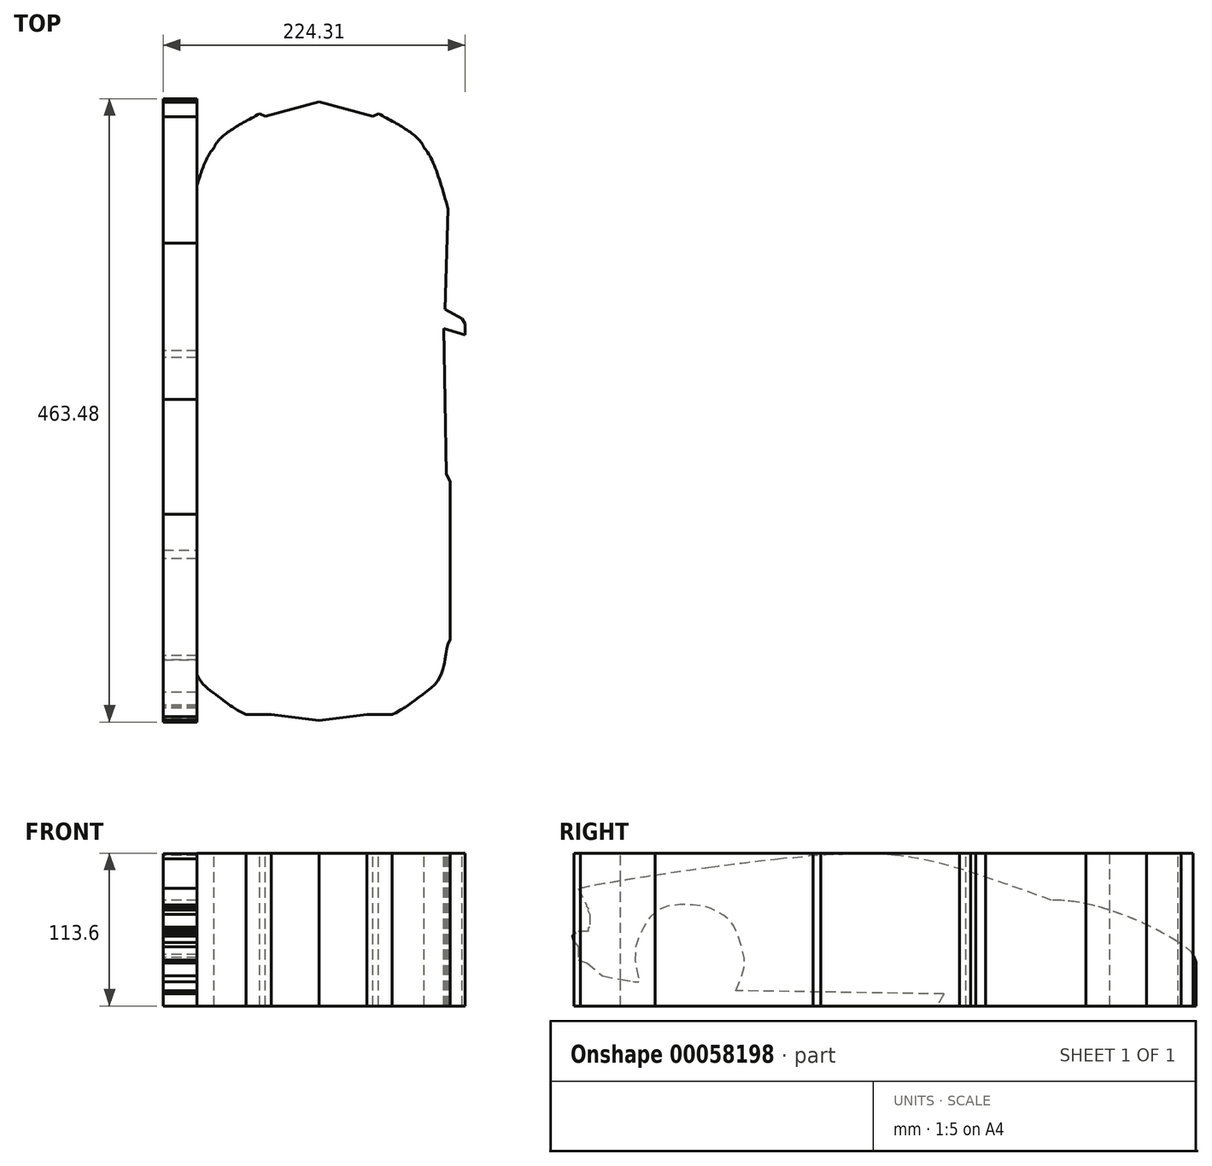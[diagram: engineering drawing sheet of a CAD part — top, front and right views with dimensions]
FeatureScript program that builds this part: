
annotation { "Feature Type Name" : "Feature", "Feature Type Description" : "" }
export const myFeature = defineFeature(function(context is Context, id is Id, definition is map)
    precondition{}
    {
        {
            var Q0;
            Q0=qCreatedBy(makeId("Right.planeOp"),FACE);
            var sketch = newSketch(context, id + "F0", { "sketchPlane" : qUnion([Q0])});
            skLineSegment(sketch, "E0.bottom", {"start": v(-232.28, 113.6) * mm, "end": v(232.28, 113.6) * mm});
            skLineSegment(sketch, "E0.top", {"start": v(-232.28, 0) * mm, "end": v(232.28, 0) * mm});
            skLineSegment(sketch, "E0.left", {"start": v(-232.28, 113.6) * mm, "end": v(-232.28, 0) * mm});
            skLineSegment(sketch, "E0.right", {"start": v(232.28, 113.6) * mm, "end": v(232.28, 0) * mm});
            skSolve(sketch);
        }
        {
            var Q0;
            Q0=makeQuery(id+"F0.imprint","IMPRINT",FACE,{"disambiguationData":[TD([[makeQuery(id+"F0.imprint","IMPRINT",EDGE,{"derivedFrom":sQuery(id+"F0.wireOp",EDGE,"E0.bottom")}),-1.0]])]});
            extrude(context, id + "F1", {"entities" : qUnion([Q0]), "depth" : 113.25 * mm});
        }
        {
            var Q0;
            Q0=makeQuery(id+"F1.opExtrude","CAP_FACE",FACE,{"disambiguationData":[OSD([sQuery(id+"F0.wireOp",EDGE,"E0.bottom"),sQuery(id+"F0.wireOp",EDGE,"E0.top"),sQuery(id+"F0.wireOp",EDGE,"E0.left"),sQuery(id+"F0.wireOp",EDGE,"E0.right")])],"isStart":true});
            extrude(context, id + "F2", {"entities" : qUnion([Q0]), "operationType" : NewBodyOperationType.ADD, "depth" : 113.25 * mm});
        }
        {
            var Q0;
            Q0=makeQuery(id+"F2.opExtrude","CAP_FACE",FACE,{"disambiguationData":[OSD([sQuery(id+"F0.wireOp",EDGE,"E0.bottom"),sQuery(id+"F0.wireOp",EDGE,"E0.top"),sQuery(id+"F0.wireOp",EDGE,"E0.left"),sQuery(id+"F0.wireOp",EDGE,"E0.right")])],"isStart":false});
            var sketch = newSketch(context, id + "F3", { "sketchPlane" : qUnion([Q0])});
            skFitSpline(sketch, "E1", {"points": [v(-163.56, 5.3) * mm, v(-228.72, 9.68) * mm, v(-231.1, 36.06) * mm, v(-229.78, 38.2) * mm, v(-227.25, 41.67) * mm, v(-112.37, 76.6) * mm, v(-33.22, -15.35) * mm], "startDerivative": vector(-140.7, 2.21) * mm, "endDerivative": vector(214.7, -339.45) * mm});
            skFitSpline(sketch, "E2", {"points": [v(-124.81, 78.57) * mm, v(-42.67, 105.83) * mm, v(3.4, 112.03) * mm, v(27.98, 106.23) * mm], "startDerivative": vector(200.5, 73.43) * mm, "endDerivative": vector(108.26, -30.3) * mm});
            skFitSpline(sketch, "E3", {"points": [v(76.57, 109.28) * mm, v(108.65, 105.55) * mm, v(139.56, 101.03) * mm, v(148.27, 98.14) * mm, v(151.76, 97.27) * mm], "startDerivative": vector(190.23, -19.18) * mm, "endDerivative": vector(22.1, -4.95) * mm});
            skFitSpline(sketch, "E4", {"points": [v(127.94, 103.12) * mm, v(190.52, 93.9) * mm, v(200.23, 92.21) * mm, v(217.48, 89.13) * mm, v(226.22, 87.48) * mm, v(230.1, 87.92) * mm], "startDerivative": vector(197.5, -27.66) * mm, "endDerivative": vector(37.14, 7.66) * mm});
            skLineSegment(sketch, "E5", {"start": v(227.03, 87.48) * mm, "end": v(220.87, 75.1) * mm});
            skLineSegment(sketch, "E6", {"start": v(220.87, 75.1) * mm, "end": v(220.87, 74.3) * mm});
            skLineSegment(sketch, "E7", {"start": v(220.87, 74.3) * mm, "end": v(219.4, 72.74) * mm});
            skLineSegment(sketch, "E8", {"start": v(219.4, 72.74) * mm, "end": v(220.14, 71.2) * mm});
            skLineSegment(sketch, "E9", {"start": v(220.14, 71.2) * mm, "end": v(218.6, 68.07) * mm});
            skLineSegment(sketch, "E10", {"start": v(218.6, 68.07) * mm, "end": v(218.6, 58.5) * mm});
            skLineSegment(sketch, "E11", {"start": v(218.6, 58.5) * mm, "end": v(219.62, 57.58) * mm});
            skLineSegment(sketch, "E12", {"start": v(219.62, 57.58) * mm, "end": v(219.62, 55.43) * mm});
            skLineSegment(sketch, "E13", {"start": v(219.62, 55.43) * mm, "end": v(225.69, 55.43) * mm});
            skLineSegment(sketch, "E14", {"start": v(225.69, 55.43) * mm, "end": v(229.6, 55.43) * mm});
            skLineSegment(sketch, "E15", {"start": v(229.6, 55.43) * mm, "end": v(228.8, 53.94) * mm});
            skLineSegment(sketch, "E16", {"start": v(228.8, 53.94) * mm, "end": v(231.2, 52.67) * mm});
            skLineSegment(sketch, "E17", {"start": v(231.2, 52.67) * mm, "end": v(231.2, 51.88) * mm});
            skLineSegment(sketch, "E18", {"start": v(231.2, 51.88) * mm, "end": v(229.7, 47.08) * mm});
            skLineSegment(sketch, "E19", {"start": v(229.7, 47.08) * mm, "end": v(227.17, 44) * mm});
            skLineSegment(sketch, "E20", {"start": v(227.17, 44) * mm, "end": v(227.17, 34.12) * mm});
            skLineSegment(sketch, "E21", {"start": v(227.17, 34.12) * mm, "end": v(220.3, 31.93) * mm});
            skLineSegment(sketch, "E22", {"start": v(220.3, 31.93) * mm, "end": v(209.05, 22.32) * mm});
            skLineSegment(sketch, "E23", {"start": v(209.05, 22.32) * mm, "end": v(184.96, 17.88) * mm});
            skLineSegment(sketch, "E24", {"start": v(184.96, 17.88) * mm, "end": v(181.82, 17.88) * mm});
            skLineSegment(sketch, "E25", {"start": v(182.43, 0) * mm, "end": v(-199.72, 0) * mm});
            skFitSpline(sketch, "E26", {"points": [v(-163.56, 5.3) * mm, v(-166.38, 8.72) * mm, v(-168.38, 13.5) * mm, v(-169.45, 17.72) * mm, v(-169.84, 22.56) * mm, v(-169.53, 28.78) * mm, v(-168.62, 37.21) * mm, v(-164.74, 48.94) * mm, v(-150.86, 62.02) * mm, v(-134.56, 67) * mm, v(-118.15, 64.81) * mm, v(-106.1, 56.9) * mm, v(-99.84, 45.94) * mm, v(-97.34, 38.54) * mm, v(-96.7, 35.47) * mm, v(-95.43, 29.36) * mm, v(-94.66, 24.21) * mm, v(-95.43, 18.32) * mm, v(-96.98, 13.15) * mm, v(-98.42, 9.35) * mm, v(-101.17, 6.92) * mm, v(-103.41, 5.98) * mm, v(-108.78, 0) * mm], "startDerivative": vector(226, -619.88) * mm, "endDerivative": vector(-0.4, -63.53) * mm});
            skLineSegment(sketch, "E27", {"start": v(-99.5, 8.1) * mm, "end": v(109.75, 11.35) * mm});
            skLineSegment(sketch, "E28", {"start": v(-165.96, 7.89) * mm, "end": v(-214.16, 7.89) * mm});
            skLineSegment(sketch, "E29", {"start": v(-214.16, 7.89) * mm, "end": v(-223.82, 8.6) * mm});
            skFitSpline(sketch, "E30", {"points": [v(109.75, 11.35) * mm, v(103.26, 32.14) * mm, v(104.34, 39.44) * mm, v(106.83, 48.57) * mm, v(109.15, 54.66) * mm, v(110.71, 58.06) * mm, v(114.45, 63.69) * mm, v(121.32, 68.97) * mm, v(127.83, 72.3) * mm, v(135.67, 74.52) * mm, v(157.74, 74.75) * mm, v(172.64, 67.4) * mm, v(182, 50.7) * mm, v(183.97, 28.46) * mm, v(181.05, 17.88) * mm], "startDerivative": vector(-140.09, 323.27) * mm, "endDerivative": vector(93.19, 542.47) * mm});
            skFitSpline(sketch, "E31", {"points": [v(-231.1, 36.06) * mm, v(-228.17, 31.08) * mm, v(-225.17, 26.94) * mm, v(-221.74, 23.48) * mm, v(-219.93, 22.5) * mm, v(-226.02, 21.78) * mm, v(-225.9, 21.77) * mm], "startDerivative": vector(8.14, -16.62) * mm, "endDerivative": vector(0, 194.68) * mm});
            skFitSpline(sketch, "E32", {"points": [v(-163.92, 7.89) * mm, v(-173.76, 7.89) * mm, v(-226.5, 10.1) * mm, v(-231.1, 36.05) * mm, v(-229.78, 38.22) * mm, v(-223.95, 44.05) * mm, v(-110.16, 76.63) * mm, v(-30.99, -15.17) * mm], "startDerivative": vector(-140.7, 2.21) * mm, "endDerivative": vector(214.62, -339.5) * mm});
            skFitSpline(sketch, "E33", {"points": [v(-223.82, 8.6) * mm, v(-227.02, 9.17) * mm, v(-228.2, 10.1) * mm, v(-227.08, 11.6) * mm, v(-219.96, 22.33) * mm, v(-222.35, 20.73) * mm, v(-222.35, 20.67) * mm, v(-238.36, 16.92) * mm], "startDerivative": vector(-35.25, 0.04) * mm, "endDerivative": vector(-69.35, -15.12) * mm});
            skFitSpline(sketch, "E34", {"points": [v(-8.7, 112) * mm, v(21.45, 112.9) * mm, v(36.26, 112.6) * mm, v(45.77, 112.25) * mm, v(56.3, 111.45) * mm, v(65.3, 110.26) * mm, v(76.57, 109.28) * mm], "startDerivative": vector(136.48, 19.32) * mm, "endDerivative": vector(30.17, -12.85) * mm});
            skLineSegment(sketch, "E35", {"start": v(-124.81, 78.57) * mm, "end": v(-126.65, 77.96) * mm});
            skSolve(sketch);
        }
        {
            var Q0;
            Q0=makeQuery(id+"F3.imprint","IMPRINT",FACE,{"disambiguationData":[TD([[makeQuery(id+"F3.imprint","IMPRINT",EDGE,{"derivedFrom":sQuery(id+"F3.wireOp",EDGE,"E2")}),1.0]])]});
            extrude(context, id + "F4", {"entities" : qUnion([Q0]), "operationType" : NewBodyOperationType.REMOVE, "oppositeDirection" : true, "depth" : 25 * mm});
        }
        {
            var Q0;
            {var subQ0=sQuery(id+"F0.wireOp",EDGE,"E0.bottom");Q0=makeQuery(id+"F2.boolean.opBoolean","MERGE",FACE,{"derivedFrom":[makeQuery(id+"F1.opExtrude","SWEPT_FACE",FACE,{"disambiguationData":[OSD([subQ0])]}),makeQuery(id+"F2.opExtrude","SWEPT_FACE",FACE,{"disambiguationData":[OSD([subQ0])]})]});}
            var sketch = newSketch(context, id + "F5", { "sketchPlane" : qUnion([Q0])});
            skLineSegment(sketch, "E36", {"start": v(98.47, 150.34) * mm, "end": v(96.04, 75.8) * mm});
            skLineSegment(sketch, "E37", {"start": v(96.04, 75.8) * mm, "end": v(109.05, 68.66) * mm});
            skLineSegment(sketch, "E38", {"start": v(109.05, 68.66) * mm, "end": v(111.06, 64.8) * mm});
            skLineSegment(sketch, "E39", {"start": v(111.06, 64.8) * mm, "end": v(111.06, 56.65) * mm});
            skLineSegment(sketch, "E40", {"start": v(111.06, 56.65) * mm, "end": v(95.33, 61.37) * mm});
            skLineSegment(sketch, "E41", {"start": v(95.33, 61.37) * mm, "end": v(97.21, -46.53) * mm});
            skLineSegment(sketch, "E42", {"start": v(97.21, -46.53) * mm, "end": v(99.93, -52.48) * mm});
            skLineSegment(sketch, "E43", {"start": v(99.93, -52.48) * mm, "end": v(99.93, -76.11) * mm});
            skLineSegment(sketch, "E44", {"start": v(99.93, -76.11) * mm, "end": v(99.93, -169.92) * mm});
            skFitSpline(sketch, "E45", {"points": [v(98.47, 150.34) * mm, v(77.1, 197.68) * mm, v(59.83, 182.23) * mm, v(46.2, 145.28) * mm], "startDerivative": vector(-48.92, 172.93) * mm, "endDerivative": vector(-31.4, -111.64) * mm});
            skLineSegment(sketch, "E46", {"start": v(42.57, 219.15) * mm, "end": v(46.64, 221.18) * mm});
            skFitSpline(sketch, "E47", {"points": [v(46.64, 221.18) * mm, v(80.67, 195.6) * mm, v(77.1, 182.72) * mm, v(72.37, 180.17) * mm], "startDerivative": vector(90.02, -47.57) * mm, "endDerivative": vector(-25.37, -7.7) * mm});
            skLineSegment(sketch, "E48", {"start": v(76.33, 202.35) * mm, "end": v(77.1, 197.68) * mm});
            skLineSegment(sketch, "E49.trimOffspring", {"start": v(80.67, 195.6) * mm, "end": v(80.67, 195.6) * mm});
            skLineSegment(sketch, "E50", {"start": v(42.57, 219.15) * mm, "end": v(2.5, 230.15) * mm});
            skFitSpline(sketch, "E51", {"points": [v(99.93, -169.92) * mm, v(96.23, -184.35) * mm, v(94.69, -191.37) * mm, v(90.58, -200.79) * mm, v(79.1, -210.89) * mm, v(70.6, -217.29) * mm, v(68.49, -218.77) * mm, v(56.76, -225.43) * mm], "startDerivative": vector(-43.18, -55.51) * mm, "endDerivative": vector(-59.67, -15.12) * mm});
            skLineSegment(sketch, "E52", {"start": v(56.76, -225.43) * mm, "end": v(38.07, -225.43) * mm});
            skLineSegment(sketch, "E53", {"start": v(38.07, -225.43) * mm, "end": v(2.5, -230.1) * mm});
            skLineSegment(sketch, "E54", {"start": v(2.5, 403.86) * mm, "end": v(2.5, -296.55) * mm});
            skLineSegment(sketch, "E55.MirrorCS", {"start": v(-37.55, 219.15) * mm, "end": v(-41.63, 221.18) * mm});
            skLineSegment(sketch, "E56.MirrorCS", {"start": v(-71.3, 202.35) * mm, "end": v(-72.08, 197.68) * mm});
            skLineSegment(sketch, "E57.MirrorCS", {"start": v(-94.92, -52.48) * mm, "end": v(-94.92, -76.11) * mm});
            skFitSpline(sketch, "E58.MirrorCS", {"points": [v(-41.63, 221.18) * mm, v(-75.66, 195.6) * mm, v(-72.08, 182.72) * mm, v(-67.35, 180.17) * mm], "startDerivative": vector(-90.02, -47.57) * mm, "endDerivative": vector(25.37, -7.7) * mm});
            skLineSegment(sketch, "E59.MirrorCS", {"start": v(-92.2, -46.53) * mm, "end": v(-94.92, -52.48) * mm});
            skLineSegment(sketch, "E60.MirrorCS", {"start": v(-106.04, 56.65) * mm, "end": v(-90.31, 61.37) * mm});
            skLineSegment(sketch, "E61.MirrorCS", {"start": v(-51.74, -225.43) * mm, "end": v(-33.05, -225.43) * mm});
            skLineSegment(sketch, "E62.MirrorCS", {"start": v(-106.04, 64.8) * mm, "end": v(-106.04, 56.65) * mm});
            skLineSegment(sketch, "E63.MirrorCS", {"start": v(-91.03, 75.8) * mm, "end": v(-104.04, 68.66) * mm});
            skLineSegment(sketch, "E64.MirrorCS", {"start": v(-104.04, 68.66) * mm, "end": v(-106.04, 64.8) * mm});
            skFitSpline(sketch, "E65.MirrorCS", {"points": [v(-94.92, -169.92) * mm, v(-91.2, -184.35) * mm, v(-89.67, -191.37) * mm, v(-85.56, -200.79) * mm, v(-74.08, -210.89) * mm, v(-65.59, -217.29) * mm, v(-63.47, -218.77) * mm, v(-51.74, -225.43) * mm], "startDerivative": vector(43.18, -55.51) * mm, "endDerivative": vector(59.67, -15.12) * mm});
            skFitSpline(sketch, "E66.MirrorCS", {"points": [v(-93.45, 150.34) * mm, v(-72.08, 197.68) * mm, v(-54.81, 182.23) * mm, v(-41.18, 145.28) * mm], "startDerivative": vector(48.92, 172.93) * mm, "endDerivative": vector(31.4, -111.64) * mm});
            skLineSegment(sketch, "E67.MirrorCS", {"start": v(-90.31, 61.37) * mm, "end": v(-92.2, -46.53) * mm});
            skLineSegment(sketch, "E68.MirrorCS", {"start": v(-75.66, 195.6) * mm, "end": v(-75.66, 195.6) * mm});
            skLineSegment(sketch, "E69.MirrorCS", {"start": v(-93.45, 150.34) * mm, "end": v(-91.03, 75.8) * mm});
            skLineSegment(sketch, "E70.MirrorCS", {"start": v(-37.55, 219.15) * mm, "end": v(2.5, 230.15) * mm});
            skLineSegment(sketch, "E71.MirrorCS", {"start": v(-94.92, -76.11) * mm, "end": v(-94.92, -169.92) * mm});
            skLineSegment(sketch, "E72.MirrorCS", {"start": v(-33.05, -225.43) * mm, "end": v(2.5, -230.1) * mm});
            skSolve(sketch);
        }
        {
            var Q0;
            {var subQ1=sQuery(id+"F5.wireOp",EDGE,"E36");Q0=makeQuery(id+"F5.imprint","IMPRINT",FACE,{"disambiguationData":[TD([[makeQuery(id+"F5.imprint","IMPRINT",EDGE,{"derivedFrom":subQ1}),1.0]])]});}
            var Q1;
            Q1=makeQuery(id+"F5.imprint","IMPRINT",FACE,{"disambiguationData":[TD([[makeQuery(id+"F5.imprint","IMPRINT",EDGE,{"derivedFrom":sQuery(id+"F5.wireOp",EDGE,"E55.MirrorCS")}),-1.0]])]});
            var Q2;
            {var subQ2=sQuery(id+"F5.wireOp",EDGE,"E61.MirrorCS");Q2=makeQuery(id+"F5.imprint","IMPRINT",FACE,{"disambiguationData":[TD([[makeQuery(id+"F5.imprint","IMPRINT",EDGE,{"derivedFrom":subQ2}),-1.0]])]});}
            extrude(context, id + "F6", {"entities" : qUnion([Q0, Q1, Q2]), "operationType" : NewBodyOperationType.REMOVE, "oppositeDirection" : true, "depth" : 1000 * mm});
        }
    });
